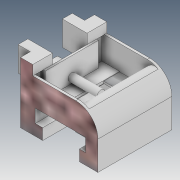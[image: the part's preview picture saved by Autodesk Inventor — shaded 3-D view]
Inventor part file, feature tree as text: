
AUTODESK INVENTOR PART (.ipt)
format: ipt  version: 2021 (Build 250183000, 183)  size: 659,456 bytes
history: native  units: in
note: dims shown in document units (in); Inventor stores cm internally (conversion verified against a paired STEP export)
features: extrude x38, sketch x38, fillet x4, other x1
ambient origin geometry x8: Origin, YZ Plane, XZ Plane, XY Plane, X Axis, Y Axis, Z Axis, Center Point
bodies: Body1 (feature_tree)
feature tree (81):
  other  "Sólido1"
  extrude  "Extrusão1"  Depth=0.1969in
  extrude  "Extrusão2"  Depth=0.3937in
  extrude  "Extrusão3"  Depth=0.0984in
  extrude  "Extrusão4"  Depth=0.1969in
  extrude  "Extrusão5"  Depth=0.3937in
  extrude  "Extrusão6"  Depth=0.0079in
  extrude  "Extrusão7"  Depth=0.0079in
  extrude  "Extrusão8"  Depth=0.0079in
  extrude  "Extrusão10"  Depth=0.0079in
  extrude  "Extrusão11"  Depth=0.0079in
  extrude  "Extrusão12"  Depth=0.0079in
  extrude  "Extrusão13"  Depth=0.0079in
  extrude  "Extrusão16"  Depth=0.0079in
  extrude  "Extrusão17"  Depth=0.1575in
  extrude  "Extrusão18"  Depth=0.0079in
  extrude  "Extrusão19"  Depth=0.0394in
  extrude  "Extrusão20"  Depth=0.0787in
  extrude  "Extrusão21"  Depth=1.1811in TaperAngle=0.0deg
  extrude  "Extrusão22"  Depth=0.3543in
  fillet  "Arredondamento1"  Radius=0.1969in
  extrude  "Extrusão23"  Depth=0.1181in TaperAngle=0.0deg
  extrude  "Extrusão24"  Depth=0.1969in TaperAngle=0.0deg
  fillet  "Arredondamento2"  Radius=0.0591in
  extrude  "Extrusão25"  Depth=0.2559in
  extrude  "Extrusão26"  Depth=0.0315in TaperAngle=0.0deg
  extrude  "Extrusão27"  Depth=0.1575in TaperAngle=0.0deg
  extrude  "Extrusão28"  Depth=0.0394in
  extrude  "Extrusão29"  Depth=0.0394in
  extrude  "Extrusão30"  Depth=0.0394in
  extrude  "Extrusão31"  Depth=0.0394in
  extrude  "Extrusão32"  Depth=0.0394in TaperAngle=0.0deg
  extrude  "Extrusão33"  Depth=0.0197in TaperAngle=0.0deg
  extrude  "Extrusão34"  Depth=0.0787in
  extrude  "Extrusão35"  Depth=0.0787in TaperAngle=0.0deg
  extrude  "Extrusão36"  Depth=0.1181in
  extrude  "Extrusão37"  Depth=0.0591in
  extrude  "Extrusão38"  Depth=0.0591in
  extrude  "Extrusão39"  Depth=0.1969in
  extrude  "Extrusão40"  Depth=0.0787in
  fillet  "Arredondamento3"  Radius=0.0394in
  fillet  "Arredondamento4"  Radius=0.0394in
  extrude  "Extrusão41"  Depth=0.1969in
  sketch  "Esboço2"  dims[d0=0.1969in d1=0.1969in]
  sketch  "Esboço4"  dims[d2=0.1181in d3=0.3937in]
  sketch  "Esboço5"  dims[d4=0.1969in d5=0.0984in]
  sketch  "Esboço6"  dims[d6=0.3937in d7=0.1969in]
  sketch  "Esboço7"  dims[d8=0.1969in d9=0.3937in]
  sketch  "Esboço8"  dims[d11=0.1969in d12=0.0079in]
  sketch  "Esboço10"  dims[d13=0.0079in d14=0.0079in]
  sketch  "Esboço12"  dims[d15=0.0079in d16=0.0079in]
  sketch  "Esboço15"  dims[d17=0.0079in d19=0.0079in]
  sketch  "Esboço16"  dims[d20=0.0079in d21=0.0079in]
  sketch  "Esboço18"  dims[d22=0.0079in d23=0.0079in]
  sketch  "Esboço20"  dims[d24=0.0079in d25=0.0079in]
  sketch  "Esboço23"  dims[d26=0.0079in d27=0.0079in]
  sketch  "Esboço25"  dims[d28=0.2756in d29=0.1575in]
  sketch  "Esboço26"  dims[d30=0.2756in d31=0.0079in]
  sketch  "Esboço28"  dims[d32=0.0787in d33=0.0394in]
  sketch  "Esboço29"  dims[d34=0.0079in d35=0.0787in]
  sketch  "Esboço30"  dims[d36=0.0394in d37=1.1811in d38=0.0in]
  sketch  "Esboço32"  dims[d39=0.4724in d40=0.3543in d46=0.1969in d47=0.0in]
  sketch  "Esboço33"  dims[d48=0.1181in d49=0.5394in d50=0.0in]
  sketch  "Esboço34"  dims[d51=0.1969in d52=0.0in d53=0.1969in d54=0.0in d55=0.0591in]
  sketch  "Esboço38"  dims[d56=0.1969in d57=0.0in d58=0.2559in]
  sketch  "Esboço39"  dims[d59=0.2559in d60=0.0315in d61=0.0in]
  sketch  "Esboço40"  dims[d62=0.1575in d63=0.0197in d64=0.0in]
  sketch  "Esboço41"  dims[d68=0.1181in d69=0.0in d70=0.0394in]
  sketch  "Esboço42"  dims[d71=0.0394in d73=0.0394in]
  sketch  "Esboço43"  dims[d74=0.3937in d75=0.0in d76=0.0394in]
  sketch  "Esboço44"  dims[d77=0.0in d78=0.0in d79=0.0394in]
  sketch  "Esboço45"  dims[d80=0.0394in d81=0.0394in d82=0.0in]
  sketch  "Esboço46"  dims[d91=0.4134in d92=0.0197in d93=0.0in]
  sketch  "Esboço47"  dims[d94=0.0157in d95=0.0in d96=0.0787in]
  sketch  "Esboço48"  dims[d97=0.0787in d98=0.0626in d99=0.0in]
  sketch  "Esboço50"  dims[d100=0.0197in d101=0.0in d102=0.1181in]
  sketch  "Esboço52"  dims[d103=0.0197in d104=0.0in d105=0.0591in]
  sketch  "Esboço53"  dims[d106=0.0591in d107=0.0591in]
  sketch  "Esboço55"  dims[d108=0.1969in d109=0.0in d110=0.0787in]
  sketch  "Esboço56"  dims[d111=0.0394in d112=0.0787in d114=0.0394in d115=0.0in d116=0.0394in]
  sketch  "Esboço57"  dims[d117=0.0591in d118=0.0591in d119=0.0984in d120=0.3543in d121=0.0in d123=0.0803in d124=0.0984in d125=0.0in d126=0.0079in d128=0.7874in d129=0.1969in d130=0.1969in d131=0.1181in d132=0.3937in d133=0.1969in d134=0.1181in d135=0.1181in d136=0.1969in d137=0.0in d138=0.0039in d139=0.0433in d140=0.0039in d141=0.3858in d142=0.0in d143=0.3937in d144=0.0in d147=0.3858in d148=0.0in d149=0.2283in d150=0.2283in d151=0.0591in d152=0.0in d153=0.0591in d154=0.0in d155=0.1969in d156=0.0in d157=0.3937in d158=0.1969in d159=0.0in d160=0.1969in d161=0.0in d163=0.1575in d164=0.1969in d165=0.0in d166=0.1969in d167=0.0in d170=0.374in d171=0.0in d172=0.1969in d173=0.0in d174=0.4724in d175=0.0in d176=0.4724in d177=0.0in d178=0.0394in d179=0.3937in d180=0.0in d181=0.3543in d182=0.1181in d183=0.1969in d184=0.0in d168=0.0197in d169=0.0344in]
